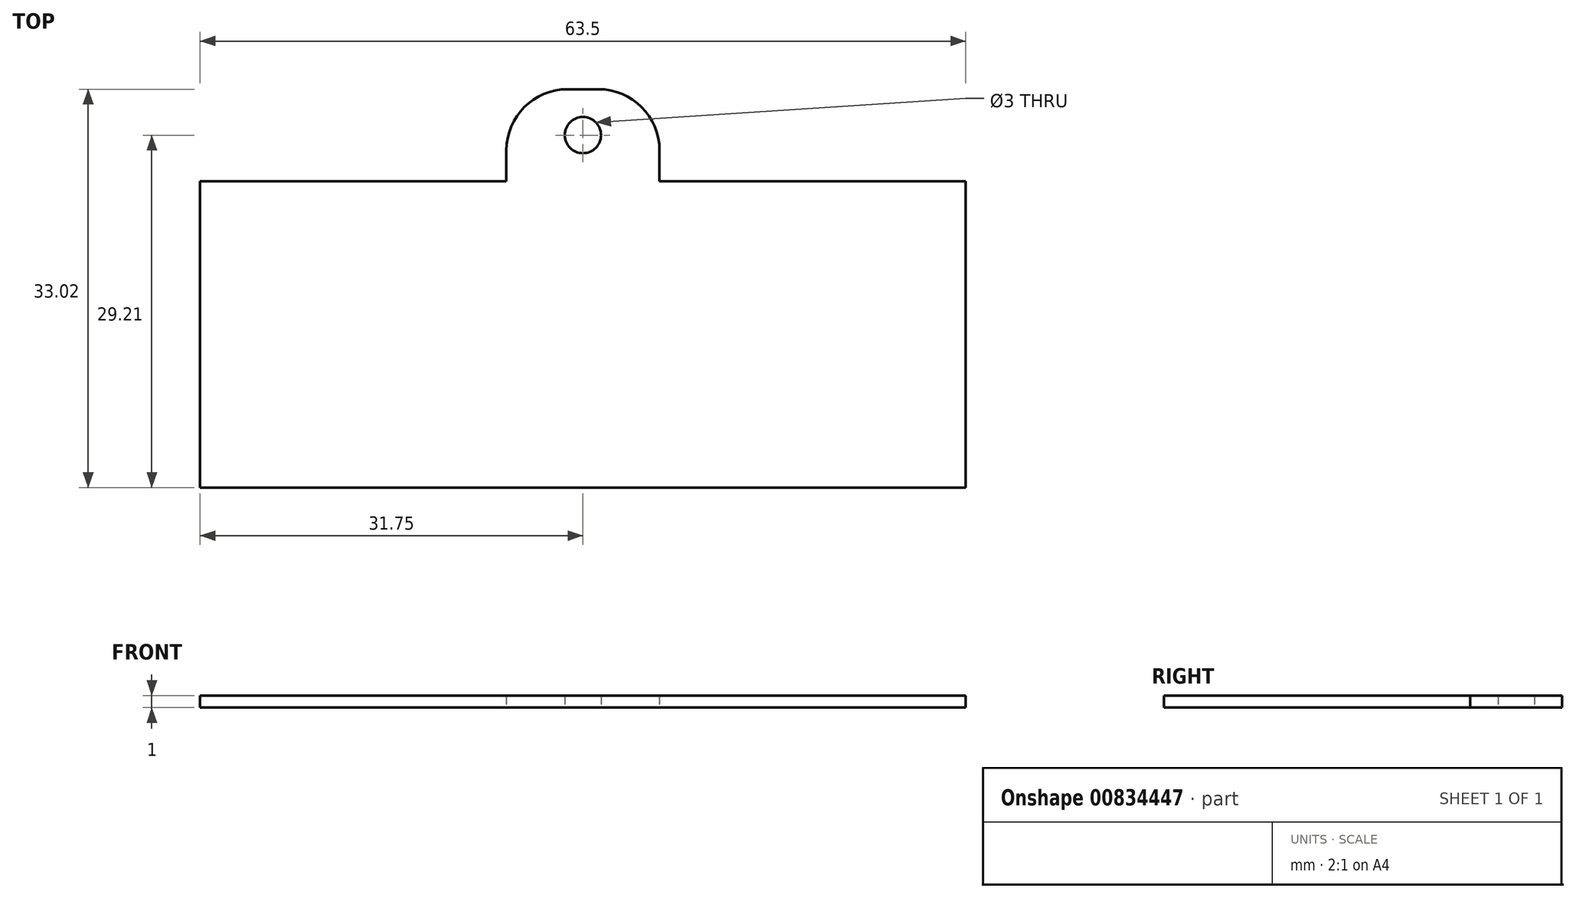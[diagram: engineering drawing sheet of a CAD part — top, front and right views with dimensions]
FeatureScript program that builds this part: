
annotation { "Feature Type Name" : "Feature", "Feature Type Description" : "" }
export const myFeature = defineFeature(function(context is Context, id is Id, definition is map)
    precondition{}
    {
        {
            var Q0;
            Q0=qCreatedBy(makeId("Top.planeOp"),FACE);
            var sketch = newSketch(context, id + "F0", { "sketchPlane" : qUnion([Q0])});
            skLineSegment(sketch, "E0.bottom", {"start": v(31.75, 12.7) * mm, "end": v(-31.75, 12.7) * mm});
            skLineSegment(sketch, "E0.top", {"start": v(31.75, -12.7) * mm, "end": v(-31.75, -12.7) * mm});
            skLineSegment(sketch, "E0.left", {"start": v(31.75, 12.7) * mm, "end": v(31.75, -12.7) * mm});
            skLineSegment(sketch, "E0.right", {"start": v(-31.75, 12.7) * mm, "end": v(-31.75, -12.7) * mm});
            skPoint(sketch, "E0.middle", {"position": v(0, 0) * mm});
            skLineSegment(sketch, "E1.bottom", {"start": v(-6.35, -12.7) * mm, "end": v(6.35, -12.7) * mm});
            skLineSegment(sketch, "E1.top", {"start": v(-6.35, -20.32) * mm, "end": v(6.35, -20.32) * mm});
            skLineSegment(sketch, "E1.left", {"start": v(-6.35, -12.7) * mm, "end": v(-6.35, -20.32) * mm});
            skLineSegment(sketch, "E1.right", {"start": v(6.35, -12.7) * mm, "end": v(6.35, -20.32) * mm});
            skPoint(sketch, "E2", {"position": v(6.35, -16.51) * mm});
            skPoint(sketch, "E3", {"position": v(0, -12.7) * mm});
            skPoint(sketch, "E4", {"position": v(31.67, -29.43) * mm});
            skLineSegment(sketch, "E5", {"start": v(6.35, -16.51) * mm, "end": v(0, -16.51) * mm});
            skCircle(sketch, "E6", {"center": v(0, -16.51) * mm, "radius": 1.5 * mm});
            skLineSegment(sketch, "E7.MirrorCS", {"start": v(-6.35, 12.7) * mm, "end": v(-6.35, 20.32) * mm});
            skLineSegment(sketch, "E8.MirrorCS", {"start": v(-6.35, 20.32) * mm, "end": v(6.35, 20.32) * mm});
            skLineSegment(sketch, "E9.MirrorCS", {"start": v(6.35, 12.7) * mm, "end": v(6.35, 20.32) * mm});
            skCircle(sketch, "E10.MirrorC", {"center": v(0, 16.51) * mm, "radius": 1.5 * mm});
            skLineSegment(sketch, "E11.MirrorCS", {"start": v(6.35, 16.51) * mm, "end": v(0, 16.51) * mm});
            skSolve(sketch);
        }
        {
            var Q0;
            {var subQ5=sQuery(id+"F0.wireOp",EDGE,"E7.MirrorCS");Q0=makeQuery(id+"F0.imprint","IMPRINT",FACE,{"disambiguationData":[TD([[makeQuery(id+"F0.imprint","IMPRINT",EDGE,{"derivedFrom":subQ5}),-1.0]])]});}
            var Q1;
            {var subQ0=sQuery(id+"F0.wireOp",EDGE,"E0.left");Q1=makeQuery(id+"F0.imprint","IMPRINT",FACE,{"disambiguationData":[TD([[makeQuery(id+"F0.imprint","IMPRINT",EDGE,{"derivedFrom":subQ0}),-1.0]])]});}
            var Q2;
            {var subQ1=sQuery(id+"F0.wireOp",EDGE,"E1.bottom");Q2=makeQuery(id+"F0.imprint","IMPRINT",FACE,{"disambiguationData":[TD([[makeQuery(id+"F0.imprint","IMPRINT",EDGE,{"derivedFrom":subQ1}),-1.0]])]});}
            extrude(context, id + "F1", {"entities" : qUnion([Q0, Q1, Q2]), "depth" : 1 * mm, "offsetDistance" : 25.4 * mm});
        }
        {
            var Q0;
            Q0=makeQuery(id+"F1.opExtrude","SWEPT_EDGE",EDGE,{"disambiguationData":[OSD([sQuery(id+"F0.wireOp",EDGE,"E8.MirrorCS"),sQuery(id+"F0.wireOp",EDGE,"E9.MirrorCS")])]});
            var Q1;
            Q1=makeQuery(id+"F1.opExtrude","SWEPT_EDGE",EDGE,{"disambiguationData":[OSD([sQuery(id+"F0.wireOp",EDGE,"E7.MirrorCS"),sQuery(id+"F0.wireOp",EDGE,"E8.MirrorCS")])]});
            var Q2;
            Q2=makeQuery(id+"F1.opExtrude","SWEPT_EDGE",EDGE,{"disambiguationData":[OSD([sQuery(id+"F0.wireOp",EDGE,"E1.top"),sQuery(id+"F0.wireOp",EDGE,"E1.left")])]});
            var Q3;
            Q3=makeQuery(id+"F1.opExtrude","SWEPT_EDGE",EDGE,{"disambiguationData":[OSD([sQuery(id+"F0.wireOp",EDGE,"E1.top"),sQuery(id+"F0.wireOp",EDGE,"E1.right")])]});
            fillet(context, id + "F2", {"entities" : qUnion([Q0, Q1, Q2, Q3]), "radius" : 5.08 * mm, "tangentPropagation" : true, "allowEdgeOverflow" : false});
        }
    });
